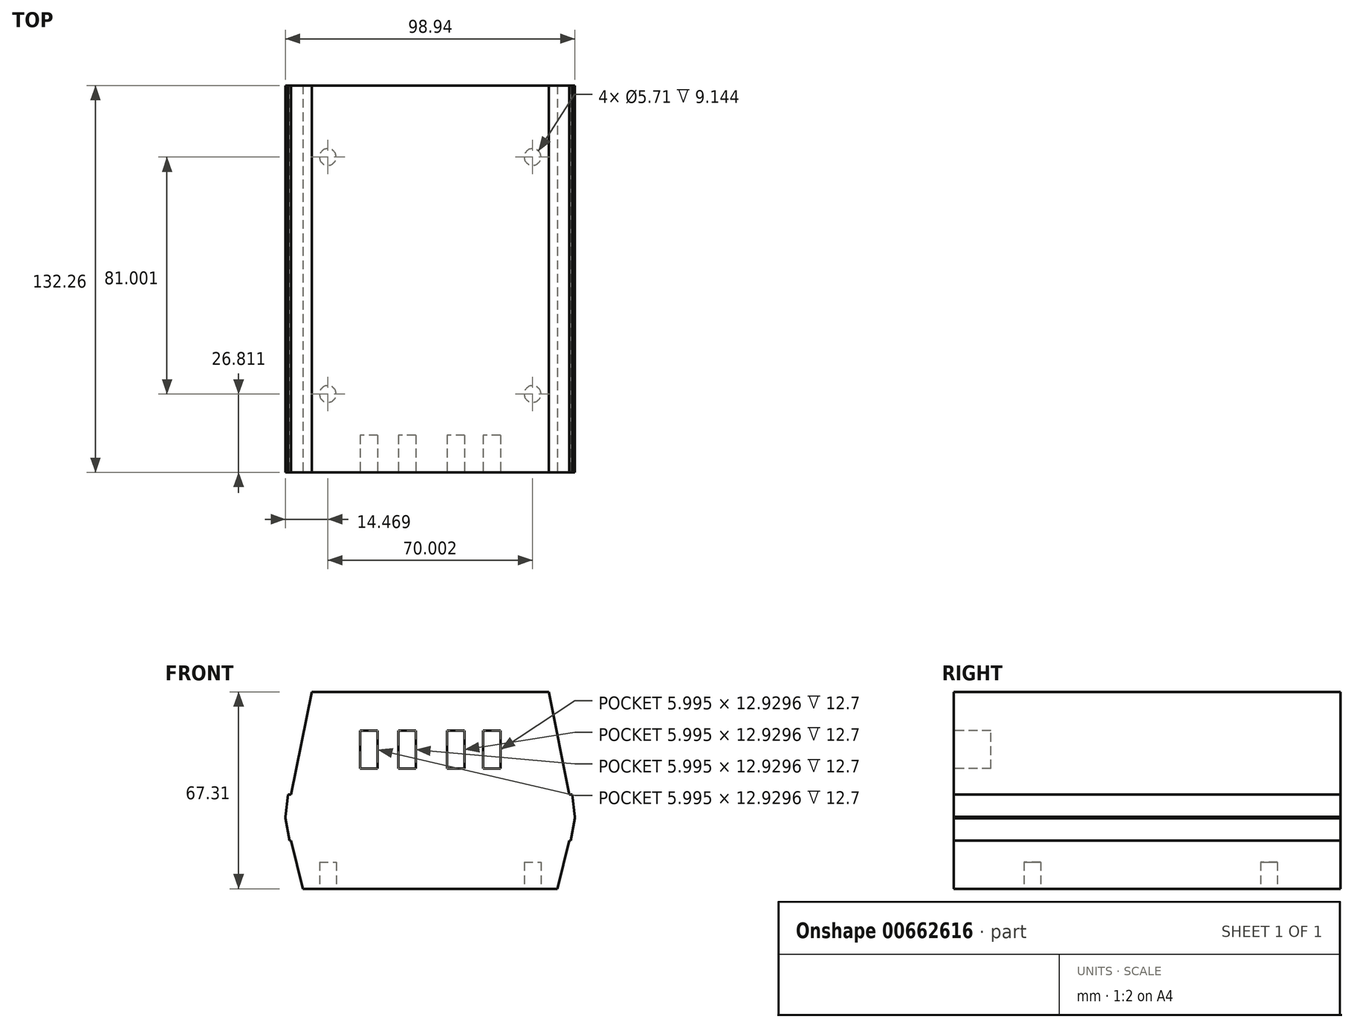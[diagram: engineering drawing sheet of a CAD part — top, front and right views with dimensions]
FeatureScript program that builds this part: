
annotation { "Feature Type Name" : "Feature", "Feature Type Description" : "" }
export const myFeature = defineFeature(function(context is Context, id is Id, definition is map)
    precondition{}
    {
        {
            var Q0;
            Q0=qCreatedBy(makeId("Top.planeOp"),FACE);
            var sketch = newSketch(context, id + "F0", { "sketchPlane" : qUnion([Q0])});
            skLineSegment(sketch, "E0.bottom", {"start": v(49.47, -66.13) * mm, "end": v(-49.47, -66.13) * mm});
            skLineSegment(sketch, "E0.top", {"start": v(49.47, 66.13) * mm, "end": v(-49.47, 66.13) * mm});
            skLineSegment(sketch, "E0.left", {"start": v(49.47, -66.13) * mm, "end": v(49.47, 66.13) * mm});
            skLineSegment(sketch, "E0.right", {"start": v(-49.47, -66.13) * mm, "end": v(-49.47, 66.13) * mm});
            skPoint(sketch, "E0.middle", {"position": v(0, 0) * mm});
            skSolve(sketch);
        }
        {
            var Q0;
            Q0 = qSketchRegion(id + "F0", true);
            extrude(context, id + "F1", {"entities" : qUnion([Q0]), "depth" : 67.3 * mm, "offsetDistance" : 25.4 * mm});
        }
        {
            var Q0;
            Q0=makeQuery(id+"F1.opExtrude","SWEPT_FACE",FACE,{"disambiguationData":[OSD([sQuery(id+"F0.wireOp",EDGE,"E0.bottom")])]});
            var sketch = newSketch(context, id + "F2", { "sketchPlane" : qUnion([Q0])});
            skLineSegment(sketch, "E1", {"start": v(-40.52, 67.31) * mm, "end": v(-47.56, 32.26) * mm});
            skLineSegment(sketch, "E2", {"start": v(-47.56, 32.26) * mm, "end": v(-48.54, 32.26) * mm});
            skLineSegment(sketch, "E3", {"start": v(-48.54, 32.26) * mm, "end": v(-49.47, 24.64) * mm});
            skLineSegment(sketch, "E4", {"start": v(-49.47, 24.64) * mm, "end": v(-49.47, 24.06) * mm});
            skLineSegment(sketch, "E5", {"start": v(-49.47, 24.06) * mm, "end": v(-48.06, 16.51) * mm});
            skLineSegment(sketch, "E6", {"start": v(-48.06, 16.51) * mm, "end": v(-47.56, 16.51) * mm});
            skLineSegment(sketch, "E7", {"start": v(-47.56, 16.51) * mm, "end": v(-43.47, 0) * mm});
            skLineSegment(sketch, "E8", {"start": v(0, 67.31) * mm, "end": v(-40.52, 67.31) * mm});
            skLineSegment(sketch, "E9", {"start": v(0, 0) * mm, "end": v(-43.47, 0) * mm});
            skLineSegment(sketch, "E10", {"start": v(0, 67.31) * mm, "end": v(0, 0) * mm, "construction": true});
            skLineSegment(sketch, "E11.MirrorCS", {"start": v(48.06, 16.51) * mm, "end": v(47.56, 16.51) * mm});
            skLineSegment(sketch, "E12.MirrorCS", {"start": v(49.47, 24.64) * mm, "end": v(49.47, 24.06) * mm});
            skLineSegment(sketch, "E13.MirrorCS", {"start": v(47.56, 32.26) * mm, "end": v(48.54, 32.26) * mm});
            skLineSegment(sketch, "E14.MirrorCS", {"start": v(47.56, 16.51) * mm, "end": v(43.47, 0) * mm});
            skLineSegment(sketch, "E15.MirrorCS", {"start": v(49.47, 24.06) * mm, "end": v(48.06, 16.51) * mm});
            skLineSegment(sketch, "E16.MirrorCS", {"start": v(48.54, 32.26) * mm, "end": v(49.47, 24.64) * mm});
            skLineSegment(sketch, "E17.MirrorCS", {"start": v(40.52, 67.31) * mm, "end": v(47.56, 32.26) * mm});
            skLineSegment(sketch, "E18.MirrorCS", {"start": v(0, 0) * mm, "end": v(43.47, 0) * mm});
            skLineSegment(sketch, "E19.MirrorCS", {"start": v(0, 67.31) * mm, "end": v(40.52, 67.31) * mm});
            skSolve(sketch);
        }
        {
            var Q0;
            {var subQ5=sQuery(id+"F2.wireOp",EDGE,"E1");Q0=makeQuery(id+"F2.imprint","IMPRINT",FACE,{"disambiguationData":[TD([[makeQuery(id+"F2.imprint","IMPRINT",EDGE,{"derivedFrom":subQ5}),-1.0]])]});}
            var Q1;
            {var subQ5=sQuery(id+"F2.wireOp",EDGE,"E5");Q1=makeQuery(id+"F2.imprint","IMPRINT",FACE,{"disambiguationData":[TD([[makeQuery(id+"F2.imprint","IMPRINT",EDGE,{"derivedFrom":subQ5}),-1.0]])]});}
            var Q2;
            Q2=makeQuery(id+"F2.imprint","IMPRINT",FACE,{"disambiguationData":[TD([[makeQuery(id+"F2.imprint","IMPRINT",EDGE,{"derivedFrom":sQuery(id+"F2.wireOp",EDGE,"E11.MirrorCS")}),1.0]])]});
            var Q3;
            Q3=makeQuery(id+"F2.imprint","IMPRINT",FACE,{"disambiguationData":[TD([[makeQuery(id+"F2.imprint","IMPRINT",EDGE,{"derivedFrom":sQuery(id+"F2.wireOp",EDGE,"E13.MirrorCS")}),1.0]])]});
            extrude(context, id + "F3", {"entities" : qUnion([Q0, Q1, Q2, Q3]), "operationType" : NewBodyOperationType.REMOVE, "endBound" : BoundingType.UP_TO_NEXT, "oppositeDirection" : true, "depth" : 25.4 * mm, "offsetDistance" : 25.4 * mm});
        }
        {
            var Q0;
            Q0=makeQuery(id+"F1.opExtrude","SWEPT_FACE",FACE,{"disambiguationData":[OSD([sQuery(id+"F0.wireOp",EDGE,"E0.bottom")])]});
            var sketch = newSketch(context, id + "F4", { "sketchPlane" : qUnion([Q0])});
            skLineSegment(sketch, "E20.bottom", {"start": v(-17.93, 41.1) * mm, "end": v(-23.92, 41.1) * mm});
            skLineSegment(sketch, "E20.top", {"start": v(-17.93, 54.02) * mm, "end": v(-23.92, 54.02) * mm});
            skLineSegment(sketch, "E20.left", {"start": v(-17.93, 41.1) * mm, "end": v(-17.93, 54.02) * mm});
            skLineSegment(sketch, "E20.right", {"start": v(-23.92, 41.1) * mm, "end": v(-23.92, 54.02) * mm});
            skPoint(sketch, "E20.middle", {"position": v(-20.92, 47.56) * mm});
            skLineSegment(sketch, "E21.bottom", {"start": v(-4.9, 41.1) * mm, "end": v(-10.9, 41.1) * mm});
            skLineSegment(sketch, "E21.top", {"start": v(-4.9, 54.02) * mm, "end": v(-10.9, 54.02) * mm});
            skLineSegment(sketch, "E21.left", {"start": v(-4.9, 41.1) * mm, "end": v(-4.9, 54.02) * mm});
            skLineSegment(sketch, "E21.right", {"start": v(-10.9, 41.1) * mm, "end": v(-10.9, 54.02) * mm});
            skPoint(sketch, "E21.middle", {"position": v(-7.9, 47.56) * mm});
            skLineSegment(sketch, "E22.bottom", {"start": v(11.77, 41.1) * mm, "end": v(5.77, 41.1) * mm});
            skLineSegment(sketch, "E22.top", {"start": v(11.77, 54.02) * mm, "end": v(5.77, 54.02) * mm});
            skLineSegment(sketch, "E22.left", {"start": v(11.77, 41.1) * mm, "end": v(11.77, 54.02) * mm});
            skLineSegment(sketch, "E22.right", {"start": v(5.77, 41.1) * mm, "end": v(5.77, 54.02) * mm});
            skPoint(sketch, "E22.middle", {"position": v(8.77, 47.56) * mm});
            skLineSegment(sketch, "E23.bottom", {"start": v(24.05, 41.1) * mm, "end": v(18.06, 41.1) * mm});
            skLineSegment(sketch, "E23.top", {"start": v(24.05, 54.02) * mm, "end": v(18.06, 54.02) * mm});
            skLineSegment(sketch, "E23.left", {"start": v(24.05, 41.1) * mm, "end": v(24.05, 54.02) * mm});
            skLineSegment(sketch, "E23.right", {"start": v(18.06, 41.1) * mm, "end": v(18.06, 54.02) * mm});
            skPoint(sketch, "E23.middle", {"position": v(21.06, 47.56) * mm});
            skSolve(sketch);
        }
        {
            var Q0;
            Q0 = qSketchRegion(id + "F4", true);
            extrude(context, id + "F5", {"entities" : qUnion([Q0]), "operationType" : NewBodyOperationType.REMOVE, "oppositeDirection" : true, "depth" : 12.7 * mm, "offsetDistance" : 25.4 * mm});
        }
        {
            var Q0;
            Q0=makeQuery(id+"F1.opExtrude","CAP_FACE",FACE,{"disambiguationData":[OSD([sQuery(id+"F0.wireOp",EDGE,"E0.bottom"),sQuery(id+"F0.wireOp",EDGE,"E0.top"),sQuery(id+"F0.wireOp",EDGE,"E0.left"),sQuery(id+"F0.wireOp",EDGE,"E0.right")])],"isStart":true});
            var sketch = newSketch(context, id + "F6", { "sketchPlane" : qUnion([Q0])});
            skLineSegment(sketch, "E24", {"start": v(0, 66.13) * mm, "end": v(0, -66.13) * mm, "construction": true});
            skLineSegment(sketch, "E25", {"start": v(-43.47, 0) * mm, "end": v(43.47, 0) * mm, "construction": true});
            skCircle(sketch, "E26.MirrorC", {"center": v(-35, -41.68) * mm, "radius": 2.86 * mm});
            skCircle(sketch, "E27.MirrorC", {"center": v(35, -41.68) * mm, "radius": 2.86 * mm});
            skCircle(sketch, "E28.MirrorC", {"center": v(35, 39.32) * mm, "radius": 2.86 * mm});
            skCircle(sketch, "E29.MirrorC", {"center": v(-35, 39.32) * mm, "radius": 2.86 * mm});
            skLineSegment(sketch, "E30", {"start": v(-35, -41.68) * mm, "end": v(0, -41.68) * mm, "construction": true});
            skLineSegment(sketch, "E31", {"start": v(0, -41.68) * mm, "end": v(35, -41.68) * mm, "construction": true});
            skSolve(sketch);
        }
        {
            var Q0;
            Q0 = qSketchRegion(id + "F6", true);
            extrude(context, id + "F7", {"entities" : qUnion([Q0]), "operationType" : NewBodyOperationType.REMOVE, "oppositeDirection" : true, "depth" : 9.14 * mm, "offsetDistance" : 25.4 * mm});
        }
    });
